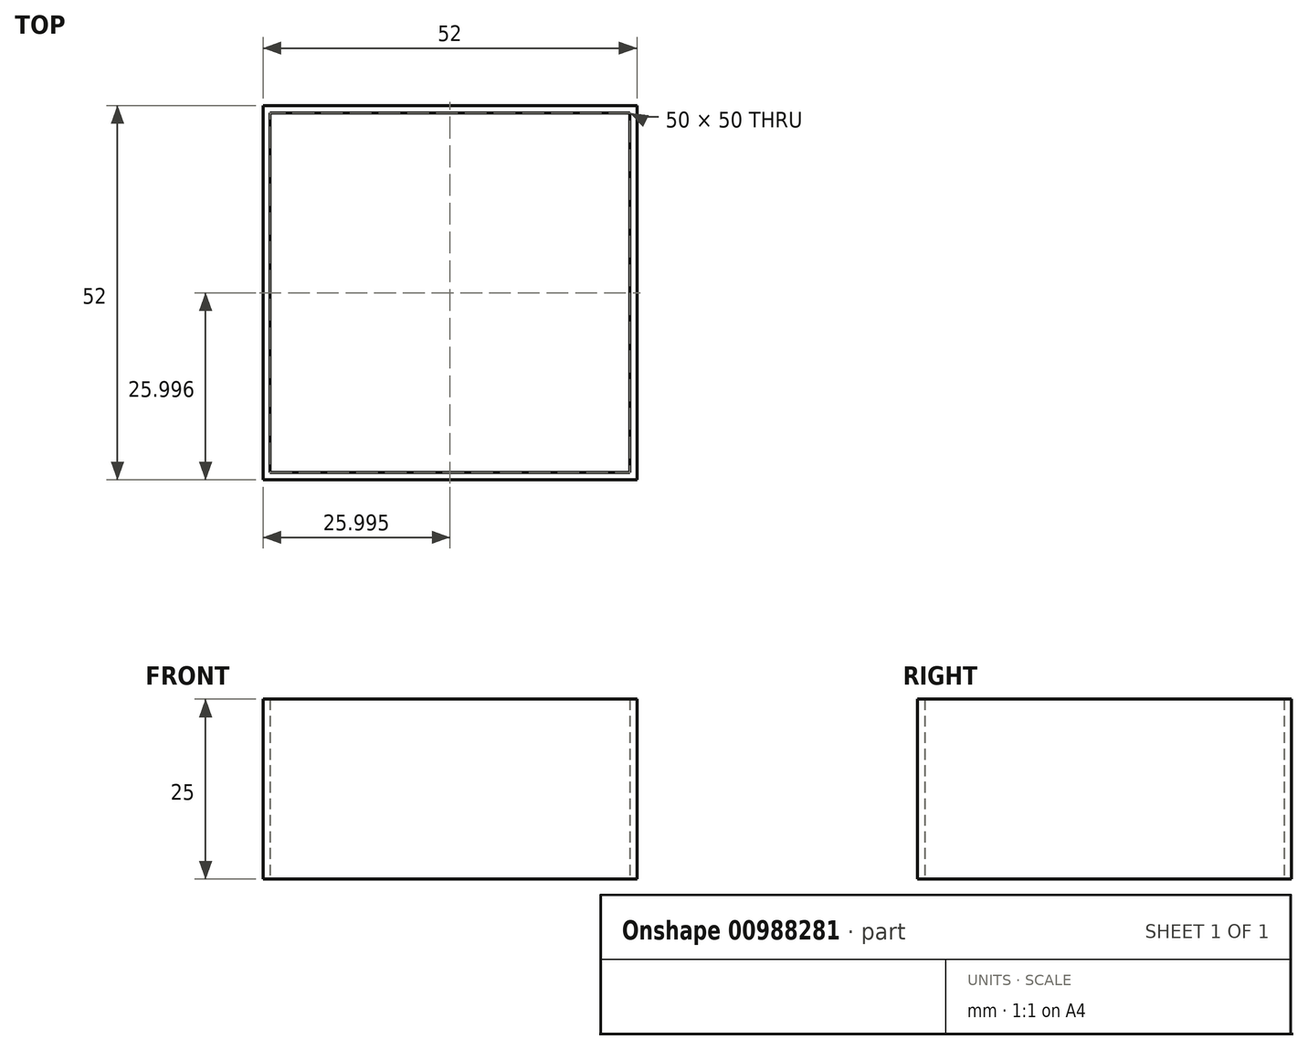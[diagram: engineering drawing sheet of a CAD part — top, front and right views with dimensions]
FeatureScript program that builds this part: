
annotation { "Feature Type Name" : "Feature", "Feature Type Description" : "" }
export const myFeature = defineFeature(function(context is Context, id is Id, definition is map)
    precondition{}
    {
        {
            var Q0;
            Q0=qCreatedBy(makeId("Top.planeOp"),FACE);
            var sketch = newSketch(context, id + "F0", { "sketchPlane" : qUnion([Q0])});
            skLineSegment(sketch, "E0.bottom", {"start": v(-26.37, 26.64) * mm, "end": v(23.63, 26.64) * mm});
            skLineSegment(sketch, "E0.top", {"start": v(-26.37, -23.36) * mm, "end": v(23.63, -23.36) * mm});
            skLineSegment(sketch, "E0.left", {"start": v(-26.37, 26.64) * mm, "end": v(-26.37, -23.36) * mm});
            skLineSegment(sketch, "E0.right", {"start": v(23.63, 26.64) * mm, "end": v(23.63, -23.36) * mm});
            skLineSegment(sketch, "E1.0", {"start": v(-27.37, 27.64) * mm, "end": v(24.63, 27.64) * mm});
            skLineSegment(sketch, "E1.1", {"start": v(-27.37, 27.64) * mm, "end": v(-27.37, -24.36) * mm});
            skLineSegment(sketch, "E1.2", {"start": v(-27.37, -24.36) * mm, "end": v(24.63, -24.36) * mm});
            skLineSegment(sketch, "E1.3", {"start": v(24.63, 27.64) * mm, "end": v(24.63, -24.36) * mm});
            skSolve(sketch);
        }
        {
            var Q0;
            Q0=makeQuery(id+"F0.imprint","IMPRINT",FACE,{"disambiguationData":[TD([[makeQuery(id+"F0.imprint","IMPRINT",EDGE,{"derivedFrom":sQuery(id+"F0.wireOp",EDGE,"E0.bottom")}),1.0]])]});
            extrude(context, id + "F1", {"entities" : qUnion([Q0]), "depth" : 25 * mm, "offsetDistance" : 25 * mm});
        }
    });
